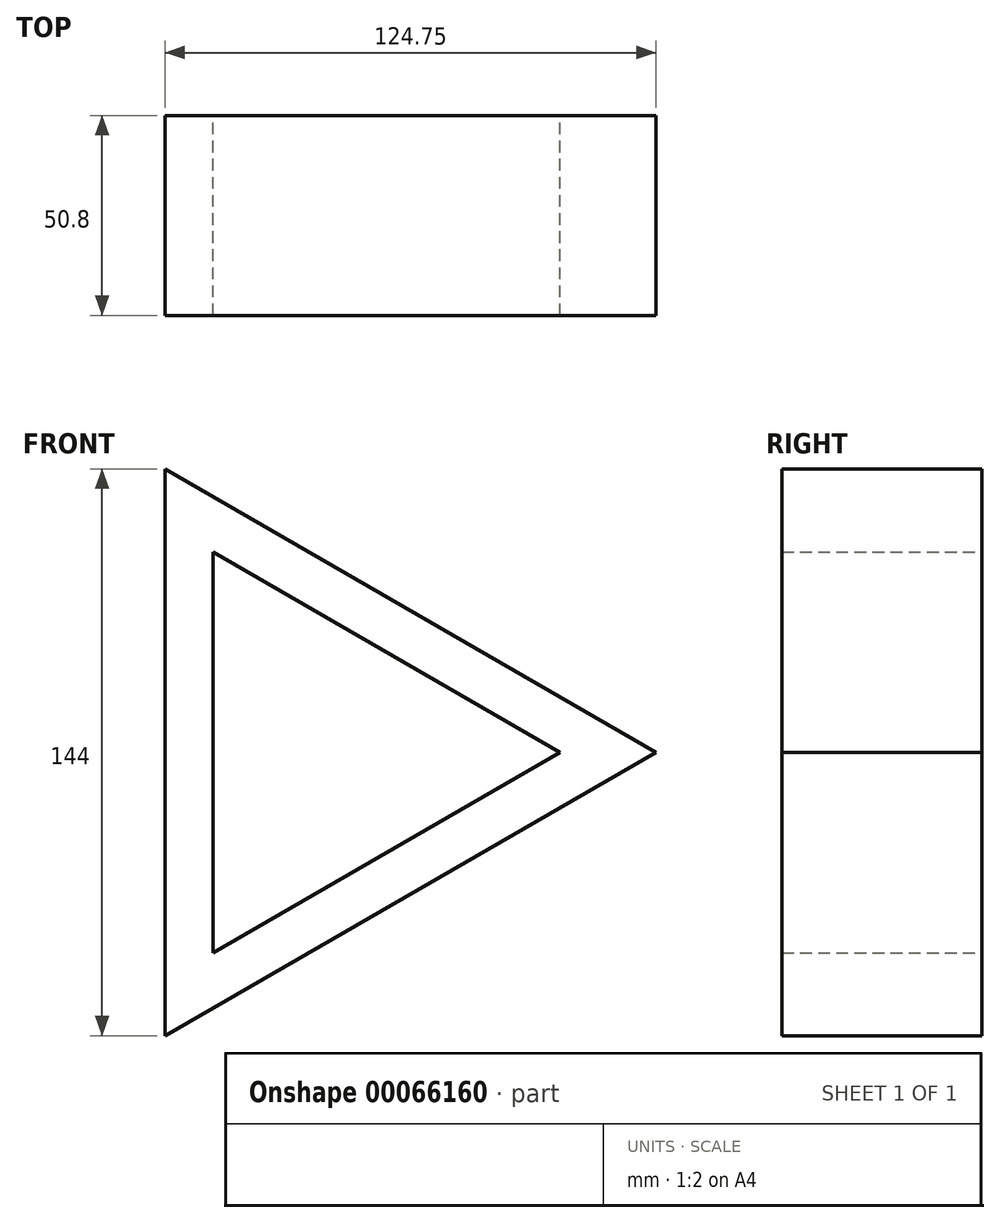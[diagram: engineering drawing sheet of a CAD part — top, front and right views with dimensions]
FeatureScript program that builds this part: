
annotation { "Feature Type Name" : "Feature", "Feature Type Description" : "" }
export const myFeature = defineFeature(function(context is Context, id is Id, definition is map)
    precondition{}
    {
        {
            var Q0;
            Q0=qCreatedBy(makeId("Front.planeOp"),FACE);
            var sketch = newSketch(context, id + "F0", { "sketchPlane" : qUnion([Q0])});
            skCircle(sketch, "E0.cCircle", {"center": v(0, 0) * mm, "radius": 41.57 * mm, "construction": true});
            skLineSegment(sketch, "E0.0", {"start": v(83.14, -0.04) * mm, "end": v(-41.6, -71.98) * mm});
            skLineSegment(sketch, "E0.1", {"start": v(-41.6, -71.98) * mm, "end": v(-41.53, 72.02) * mm});
            skLineSegment(sketch, "E0.2", {"start": v(-41.53, 72.02) * mm, "end": v(83.14, -0.04) * mm});
            skPoint(sketch, "E0.0.midPoint", {"position": v(20.77, -36.01) * mm});
            skSolve(sketch);
        }
        {
            var Q0;
            Q0=qCreatedBy(makeId("Front.planeOp"),FACE);
            var sketch = newSketch(context, id + "F1", { "sketchPlane" : qUnion([Q0])});
            skCircle(sketch, "E1.cCircle", {"center": v(0, 0) * mm, "radius": 29.38 * mm, "construction": true});
            skLineSegment(sketch, "E1.0", {"start": v(-29.38, -50.89) * mm, "end": v(-29.38, 50.89) * mm});
            skLineSegment(sketch, "E1.1", {"start": v(-29.38, 50.89) * mm, "end": v(58.76, 0) * mm});
            skLineSegment(sketch, "E1.2", {"start": v(58.76, 0) * mm, "end": v(-29.38, -50.89) * mm});
            skPoint(sketch, "E1.0.midPoint", {"position": v(-29.38, 0) * mm});
            skSolve(sketch);
        }
        {
            var Q0;
            Q0=makeQuery(id+"F1.imprint","IMPRINT",FACE,{"disambiguationData":[TD([[makeQuery(id+"F1.imprint","IMPRINT",EDGE,{"derivedFrom":sQuery(id+"F1.wireOp",EDGE,"E1.0")}),-1.0]])]});
            var Q1;
            Q1=makeQuery(id+"F0.imprint","IMPRINT",FACE,{"disambiguationData":[TD([[makeQuery(id+"F0.imprint","IMPRINT",EDGE,{"derivedFrom":sQuery(id+"F0.wireOp",EDGE,"E0.0")}),-1.0]])]});
            extrude(context, id + "F2", {"entities" : qUnion([Q0, Q1]), "depth" : 50.8 * mm});
        }
    });
